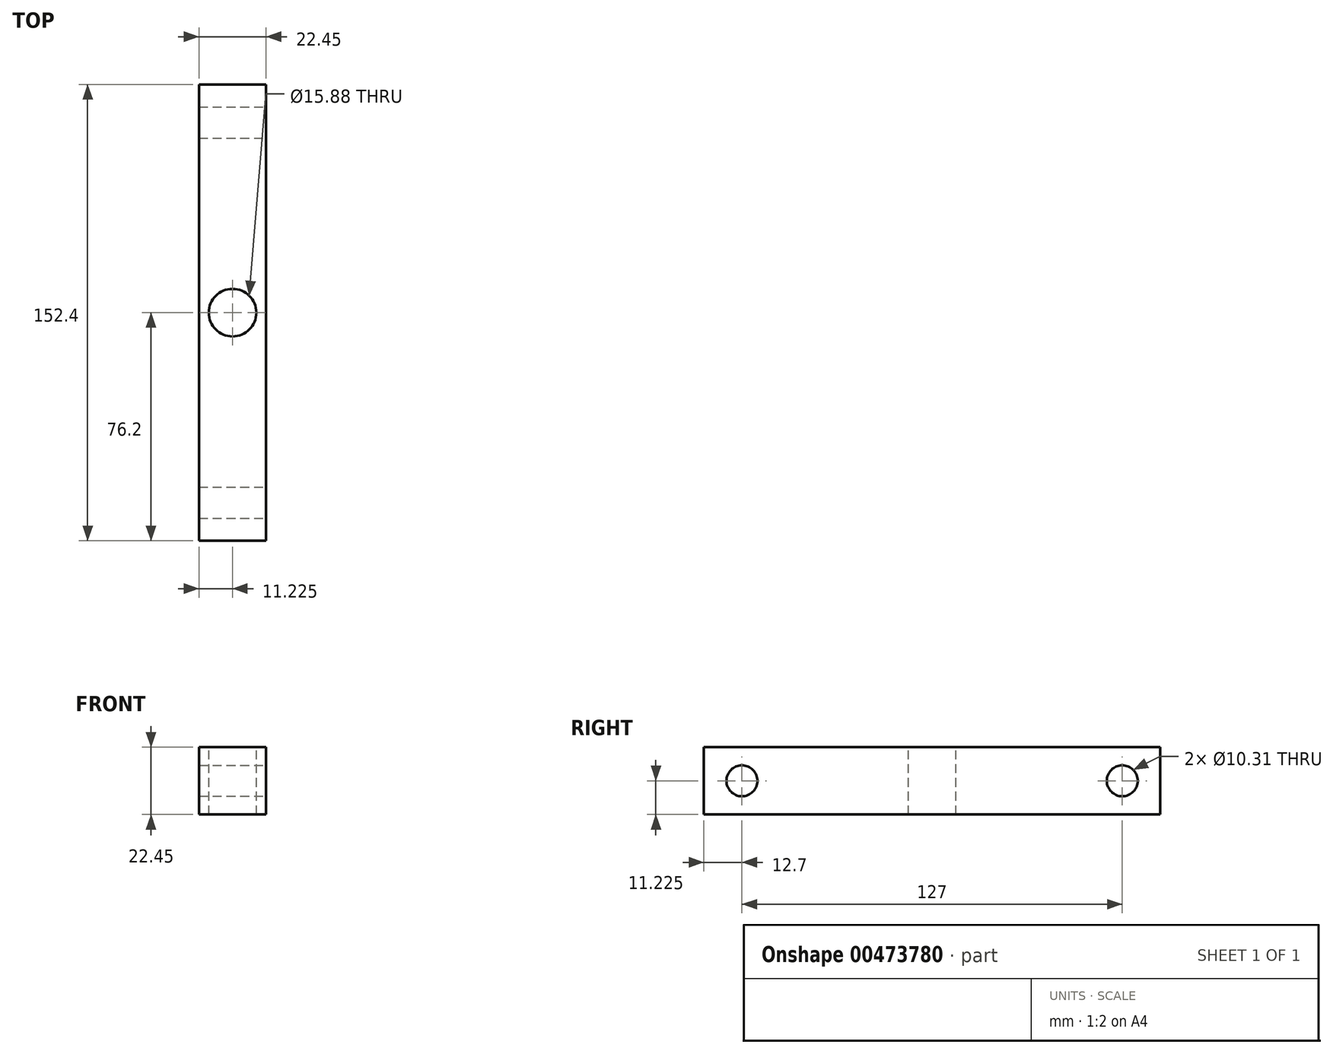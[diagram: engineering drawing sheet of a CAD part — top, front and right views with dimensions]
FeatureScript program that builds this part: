
annotation { "Feature Type Name" : "Feature", "Feature Type Description" : "" }
export const myFeature = defineFeature(function(context is Context, id is Id, definition is map)
    precondition{}
    {
        {
            var Q0;
            Q0=qCreatedBy(makeId("Front.planeOp"),FACE);
            var sketch = newSketch(context, id + "F0", { "sketchPlane" : qUnion([Q0])});
            skLineSegment(sketch, "E0.bottom", {"start": v(15.86, 14.62) * mm, "end": v(38.31, 14.62) * mm});
            skLineSegment(sketch, "E0.top", {"start": v(15.86, 37.07) * mm, "end": v(38.31, 37.07) * mm});
            skLineSegment(sketch, "E0.left", {"start": v(15.86, 14.62) * mm, "end": v(15.86, 37.07) * mm});
            skLineSegment(sketch, "E0.right", {"start": v(38.31, 14.62) * mm, "end": v(38.31, 37.07) * mm});
            skSolve(sketch);
        }
        {
            var Q0;
            Q0 = qSketchRegion(id + "F0", true);
            extrude(context, id + "F1", {"entities" : qUnion([Q0]), "depth" : 152.4 * mm});
        }
        {
            var Q0;
            Q0=makeQuery(id+"F1.opExtrude","SWEPT_FACE",FACE,{"disambiguationData":[OSD([sQuery(id+"F0.wireOp",EDGE,"E0.top")])]});
            var sketch = newSketch(context, id + "F2", { "sketchPlane" : qUnion([Q0])});
            skLineSegment(sketch, "E1", {"start": v(15.86, -76.2) * mm, "end": v(38.31, -76.2) * mm, "construction": true});
            skCircle(sketch, "E2", {"center": v(27.08, -76.2) * mm, "radius": 7.94 * mm});
            skSolve(sketch);
        }
        {
            var Q0;
            Q0 = qSketchRegion(id + "F2", true);
            extrude(context, id + "F3", {"entities" : qUnion([Q0]), "operationType" : NewBodyOperationType.REMOVE, "endBound" : BoundingType.THROUGH_ALL, "oppositeDirection" : true, "depth" : 25.4 * mm});
        }
        {
            var Q0;
            Q0=makeQuery(id+"F1.opExtrude","SWEPT_FACE",FACE,{"disambiguationData":[OSD([sQuery(id+"F0.wireOp",EDGE,"E0.right")])]});
            var sketch = newSketch(context, id + "F4", { "sketchPlane" : qUnion([Q0])});
            skLineSegment(sketch, "E3", {"start": v(-152.4, 25.84) * mm, "end": v(0, 25.84) * mm, "construction": true});
            skCircle(sketch, "E4", {"center": v(-139.7, 25.84) * mm, "radius": 5.16 * mm});
            skCircle(sketch, "E5", {"center": v(-12.7, 25.84) * mm, "radius": 5.16 * mm});
            skSolve(sketch);
        }
        {
            var Q0;
            Q0 = qSketchRegion(id + "F4", true);
            extrude(context, id + "F5", {"entities" : qUnion([Q0]), "operationType" : NewBodyOperationType.REMOVE, "endBound" : BoundingType.THROUGH_ALL, "oppositeDirection" : true, "depth" : 25.4 * mm});
        }
    });
